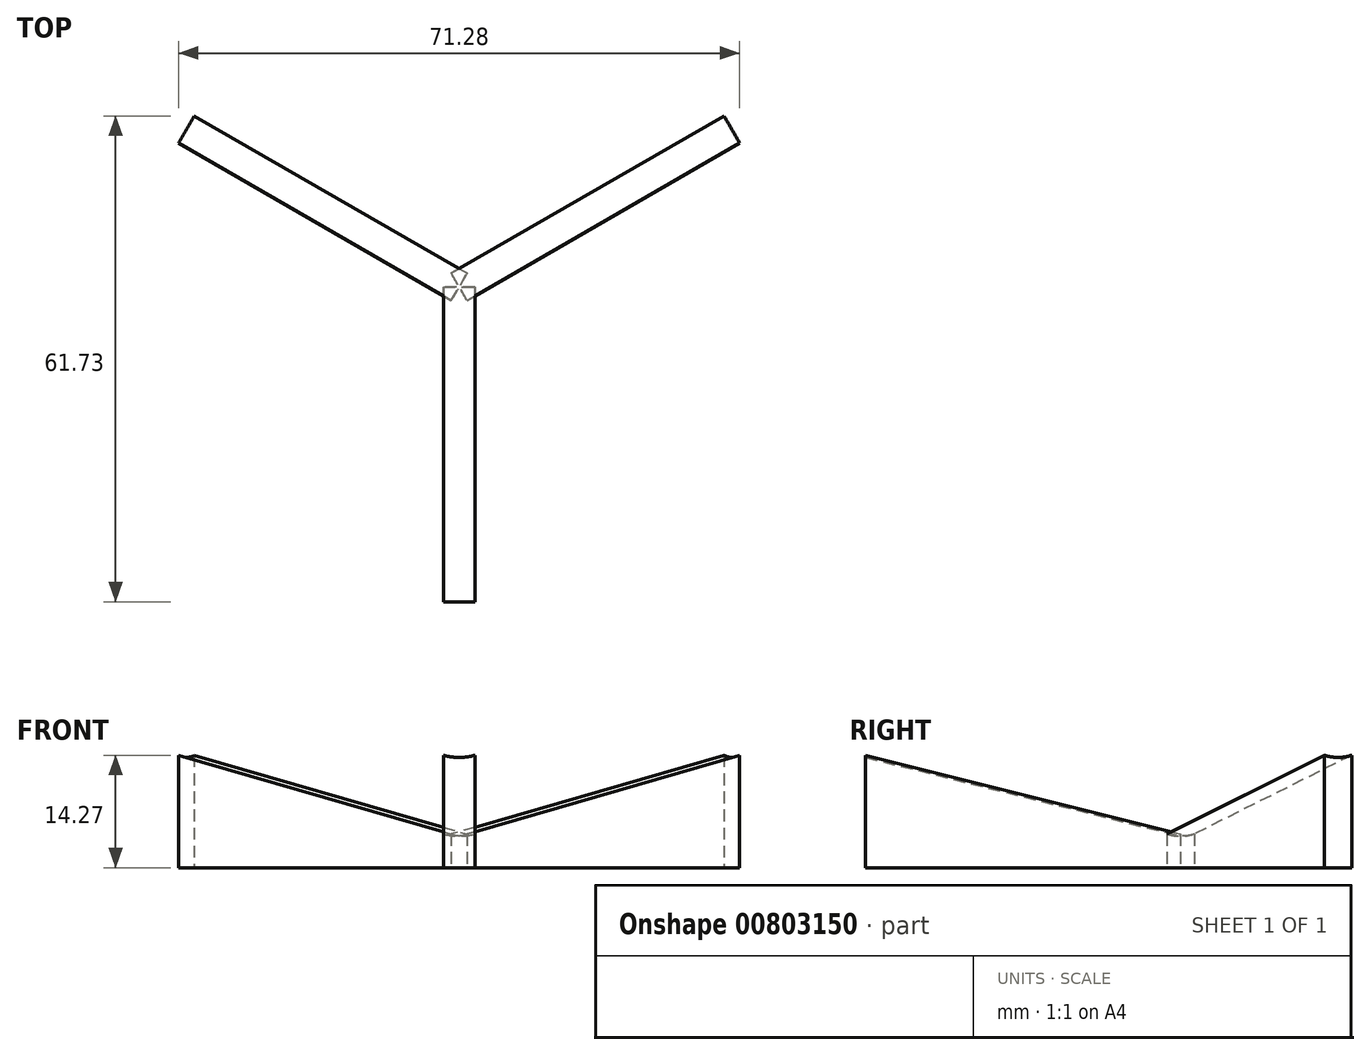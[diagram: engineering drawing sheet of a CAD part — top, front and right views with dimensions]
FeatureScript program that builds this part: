
annotation { "Feature Type Name" : "Feature", "Feature Type Description" : "" }
export const myFeature = defineFeature(function(context is Context, id is Id, definition is map)
    precondition{}
    {
        {
            var Q0;
            Q0=qCreatedBy(makeId("Front.planeOp"),FACE);
            var sketch = newSketch(context, id + "F0", { "sketchPlane" : qUnion([Q0])});
            skCircle(sketch, "E0", {"center": v(0, 11.5) * mm, "radius": 7.5 * mm, "construction": true});
            skLineSegment(sketch, "E1", {"start": v(-2, 4.27) * mm, "end": v(-2, 0) * mm});
            skLineSegment(sketch, "E2", {"start": v(2, 4.27) * mm, "end": v(2, 0) * mm});
            skLineSegment(sketch, "E3", {"start": v(2, 0) * mm, "end": v(-2, 0) * mm});
            skPoint(sketch, "E4", {"position": v(0, 4) * mm});
            skArc(sketch, "E5", {"start": v(-2, 4.27) * mm, "mid": v(0, 4) * mm, "end": v(2, 4.27) * mm});
            skPoint(sketch, "E6", {"position": v(0, 0) * mm});
            skLineSegment(sketch, "E7", {"start": v(0, 0) * mm, "end": v(0, 4) * mm, "construction": true});
            skSolve(sketch);
        }
        {
            var Q0;
            Q0=qCreatedBy(makeId("Front.planeOp"),FACE);
            cPlane(context, id + "F1", {"entities" : qUnion([Q0]), "cplaneType" : CPlaneType.OFFSET, "offset" : 40 * mm, "width" : 150 * mm, "height" : 150 * mm});
        }
        {
            var Q0;
            Q0=qCreatedBy(id+"F1.planeOp",FACE);
            var sketch = newSketch(context, id + "F2", { "sketchPlane" : qUnion([Q0])});
            skCircle(sketch, "E8", {"center": v(0, 21.5) * mm, "radius": 7.5 * mm, "construction": true});
            skLineSegment(sketch, "E9", {"start": v(-2, 14.27) * mm, "end": v(-2, 0) * mm});
            skLineSegment(sketch, "E10", {"start": v(2, 14.27) * mm, "end": v(2, 0) * mm});
            skLineSegment(sketch, "E11", {"start": v(2, 0) * mm, "end": v(-2, 0) * mm});
            skArc(sketch, "E12", {"start": v(-2, 14.27) * mm, "mid": v(0, 14) * mm, "end": v(2, 14.27) * mm});
            skPoint(sketch, "E13", {"position": v(0, 0) * mm});
            skPoint(sketch, "E14", {"position": v(0, 14) * mm});
            skSolve(sketch);
        }
        {
            var Q0;
            Q0=makeQuery(id+"F0.imprint","IMPRINT",FACE,{"disambiguationData":[TD([[makeQuery(id+"F0.imprint","IMPRINT",EDGE,{"derivedFrom":sQuery(id+"F0.wireOp",EDGE,"E1")}),1.0]])]});
            var Q1;
            Q1=makeQuery(id+"F2.imprint","IMPRINT",FACE,{"disambiguationData":[TD([[makeQuery(id+"F2.imprint","IMPRINT",EDGE,{"derivedFrom":sQuery(id+"F2.wireOp",EDGE,"E9")}),1.0]])]});
            loft(context, id + "F3", {"sheetProfilesArray" : [{ "sheetProfileEntities" : qUnion([Q0]) }, { "sheetProfileEntities" : qUnion([Q1]) }]});
        }
        {
            var Q0;
            Q0=makeQuery(id+"F3.opLoft","SWEPT_BODY",BODY,{"disambiguationData":[OSD([makeQuery(id+"F0.imprint","IMPRINT",FACE,{"disambiguationData":[TD([[makeQuery(id+"F0.imprint","IMPRINT",EDGE,{"derivedFrom":sQuery(id+"F0.wireOp",EDGE,"E1")}),1.0]])]}),makeQuery(id+"F2.imprint","IMPRINT",FACE,{"disambiguationData":[TD([[makeQuery(id+"F2.imprint","IMPRINT",EDGE,{"derivedFrom":sQuery(id+"F2.wireOp",EDGE,"E9")}),1.0]])]})])]});
            var Q1;
            Q1=sQuery(id+"F0.wireOp",EDGE,"E7");
            circularPattern(context, id + "F4", {"entities" : qUnion([Q0]), "axis" : qUnion([Q1]), "angle" : 360 * degree, "instanceCount" : 3, "equalSpace" : true});
        }
    });
